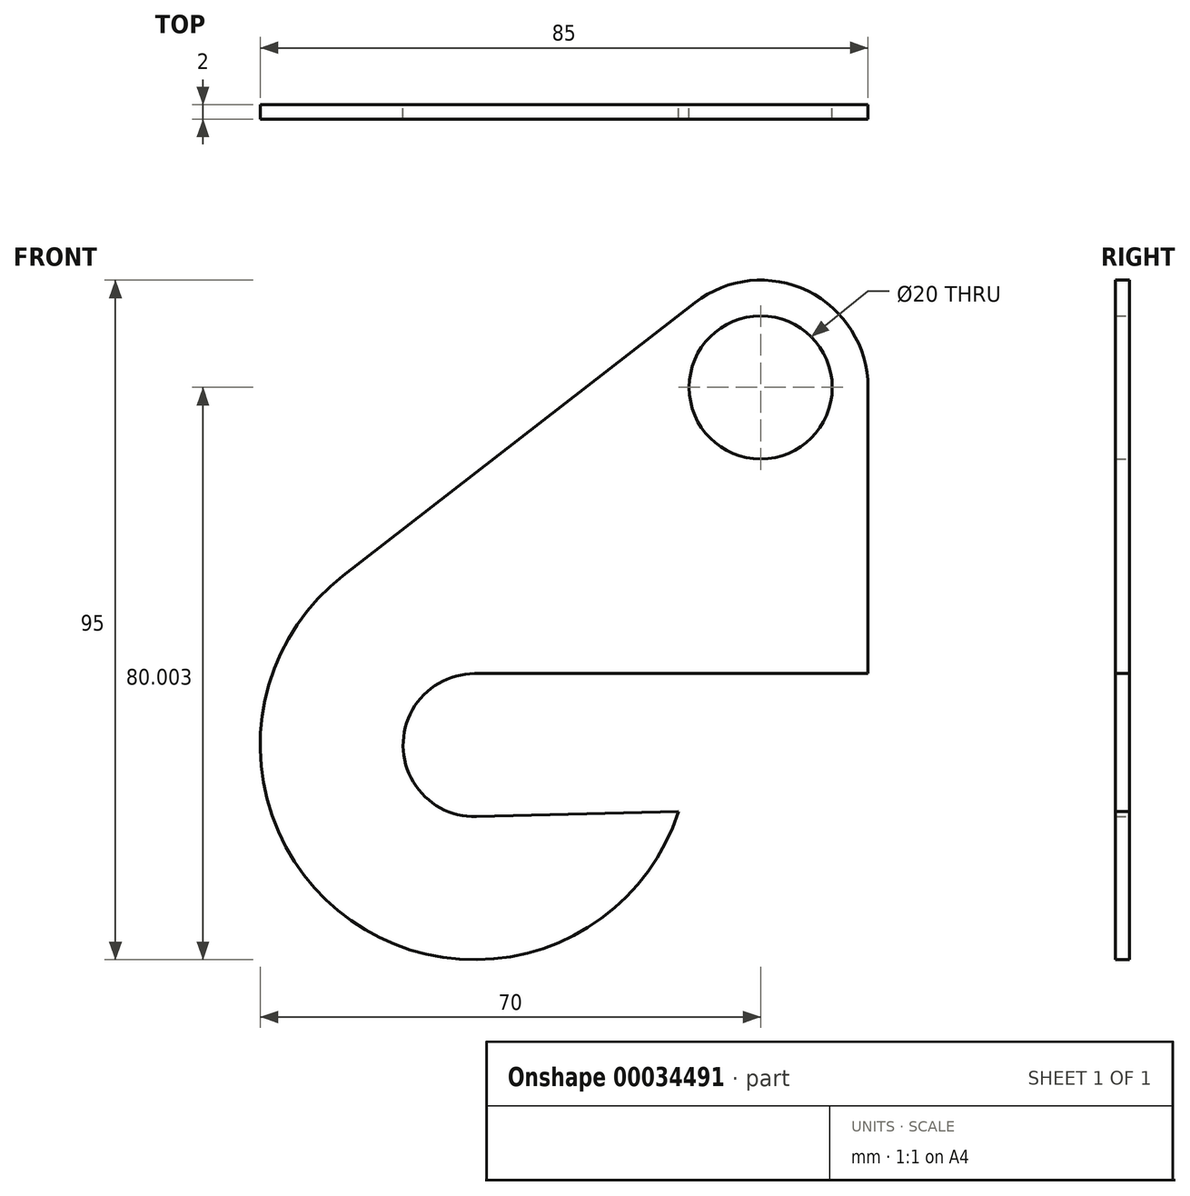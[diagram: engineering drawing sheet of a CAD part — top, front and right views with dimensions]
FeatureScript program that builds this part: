
annotation { "Feature Type Name" : "Feature", "Feature Type Description" : "" }
export const myFeature = defineFeature(function(context is Context, id is Id, definition is map)
    precondition{}
    {
        {
            var Q0;
            Q0=qCreatedBy(makeId("Front.planeOp"),FACE);
            var sketch = newSketch(context, id + "F0", { "sketchPlane" : qUnion([Q0])});
            skArc(sketch, "E0", {"start": v(-15.87, -15.83) * mm, "mid": v(-74.15, -26.2) * mm, "end": v(-15.62, -35.11) * mm});
            skArc(sketch, "E1", {"start": v(-44.15, -15.83) * mm, "mid": v(-54.15, -25.95) * mm, "end": v(-43.9, -35.82) * mm});
            skCircle(sketch, "E2", {"center": v(-4.15, 24.17) * mm, "radius": 15 * mm});
            skLineSegment(sketch, "E3", {"start": v(-62.53, -2.12) * mm, "end": v(-10.9, 37.93) * mm});
            skLineSegment(sketch, "E4", {"start": v(10.85, 24.17) * mm, "end": v(10.85, -15.83) * mm});
            skLineSegment(sketch, "E5", {"start": v(-44.15, -15.83) * mm, "end": v(10.85, -15.83) * mm});
            skLineSegment(sketch, "E6", {"start": v(-43.9, -35.82) * mm, "end": v(-15.62, -35.11) * mm});
            skCircle(sketch, "E7", {"center": v(-4.15, 24.17) * mm, "radius": 10 * mm});
            skSolve(sketch);
        }
        {
            var Q0;
            {var subQ1=sQuery(id+"F0.wireOp",EDGE,"E4");Q0=makeQuery(id+"F0.imprint","IMPRINT",FACE,{"disambiguationData":[TD([[makeQuery(id+"F0.imprint","IMPRINT",EDGE,{"derivedFrom":subQ1}),-1.0]])]});}
            var Q1;
            Q1=makeQuery(id+"F0.imprint","IMPRINT",FACE,{"disambiguationData":[TD([[makeQuery(id+"F0.imprint","IMPRINT",EDGE,{"derivedFrom":sQuery(id+"F0.wireOp",EDGE,"E7")}),-1.0]])]});
            var Q2;
            {var subQ5=sQuery(id+"F0.wireOp",EDGE,"E1");Q2=makeQuery(id+"F0.imprint","IMPRINT",FACE,{"disambiguationData":[TD([[makeQuery(id+"F0.imprint","IMPRINT",EDGE,{"derivedFrom":subQ5}),-1.0]])]});}
            extrude(context, id + "F1", {"entities" : qUnion([Q0, Q1, Q2]), "depth" : 2 * mm});
        }
    });
